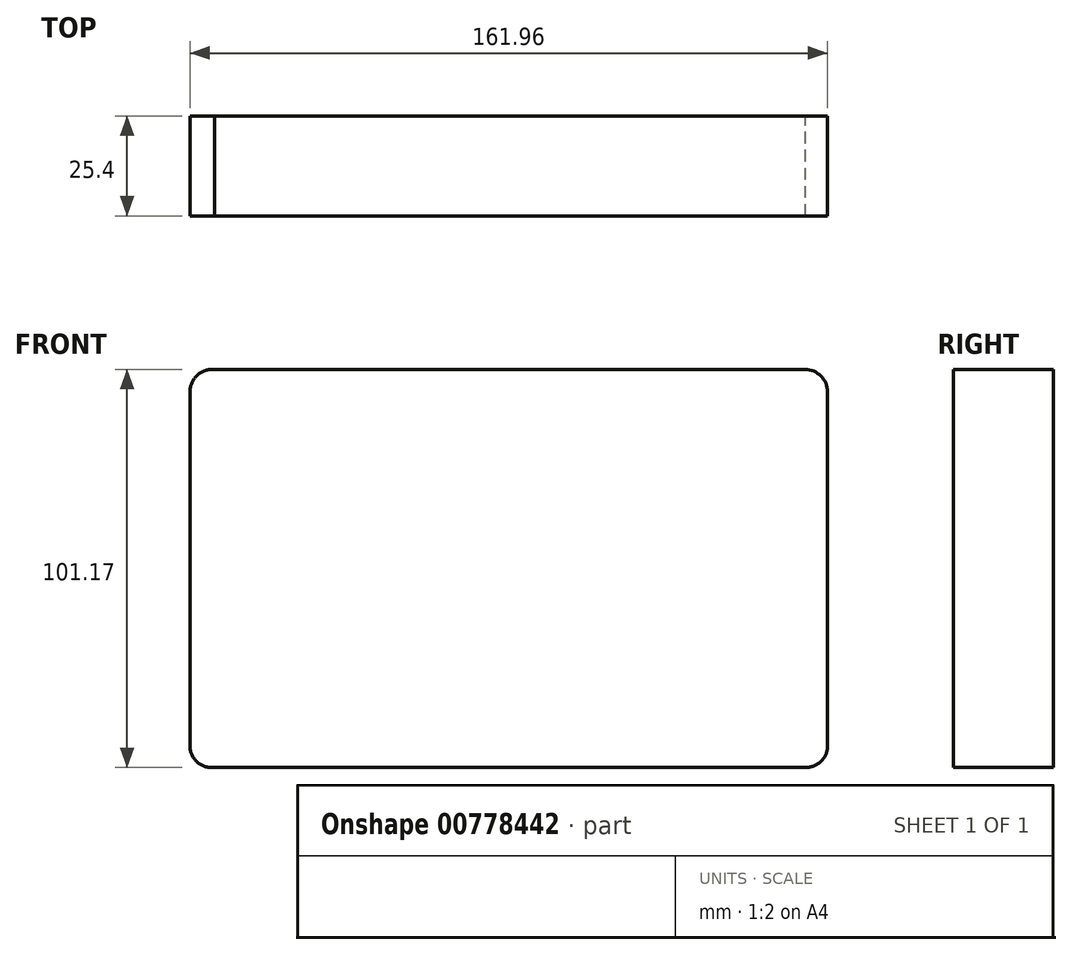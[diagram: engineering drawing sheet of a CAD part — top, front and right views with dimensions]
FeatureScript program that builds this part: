
annotation { "Feature Type Name" : "Feature", "Feature Type Description" : "" }
export const myFeature = defineFeature(function(context is Context, id is Id, definition is map)
    precondition{}
    {
        {
            var Q0;
            Q0=qCreatedBy(makeId("Front.planeOp"),FACE);
            var sketch = newSketch(context, id + "F0", { "sketchPlane" : qUnion([Q0])});
            skLineSegment(sketch, "E0", {"start": v(-79.38, 74.15) * mm, "end": v(70.62, 74.15) * mm});
            skLineSegment(sketch, "E1", {"start": v(-79.27, -26.92) * mm, "end": v(70.73, -26.92) * mm});
            skLineSegment(sketch, "E2", {"start": v(-85.64, 68.46) * mm, "end": v(-85.64, -21.54) * mm});
            skLineSegment(sketch, "E3", {"start": v(76.32, 68.46) * mm, "end": v(76.32, -21.54) * mm});
            skArc(sketch, "E4", {"start": v(-79.38, 74.15) * mm, "mid": v(-83.77, 72.69) * mm, "end": v(-85.64, 68.46) * mm});
            skArc(sketch, "E5", {"start": v(76.32, 68.46) * mm, "mid": v(74.64, 72.48) * mm, "end": v(70.62, 74.15) * mm});
            skArc(sketch, "E6", {"start": v(-85.64, -21.54) * mm, "mid": v(-83.7, -25.7) * mm, "end": v(-79.27, -26.92) * mm});
            skArc(sketch, "E7", {"start": v(70.73, -26.92) * mm, "mid": v(74.67, -25.42) * mm, "end": v(76.32, -21.54) * mm});
            skSolve(sketch);
        }
        {
            var Q0;
            Q0 = qSketchRegion(id + "F0", true);
            extrude(context, id + "F1", {"entities" : qUnion([Q0]), "depth" : 25.4 * mm, "offsetDistance" : 25.4 * mm});
        }
        {
            var Q0;
            Q0 = qSketchRegion(id + "F0", true);
            extrude(context, id + "F2", {"entities" : qUnion([Q0]), "operationType" : NewBodyOperationType.ADD, "depth" : 25 * mm, "offsetDistance" : 25 * mm});
        }
    });
